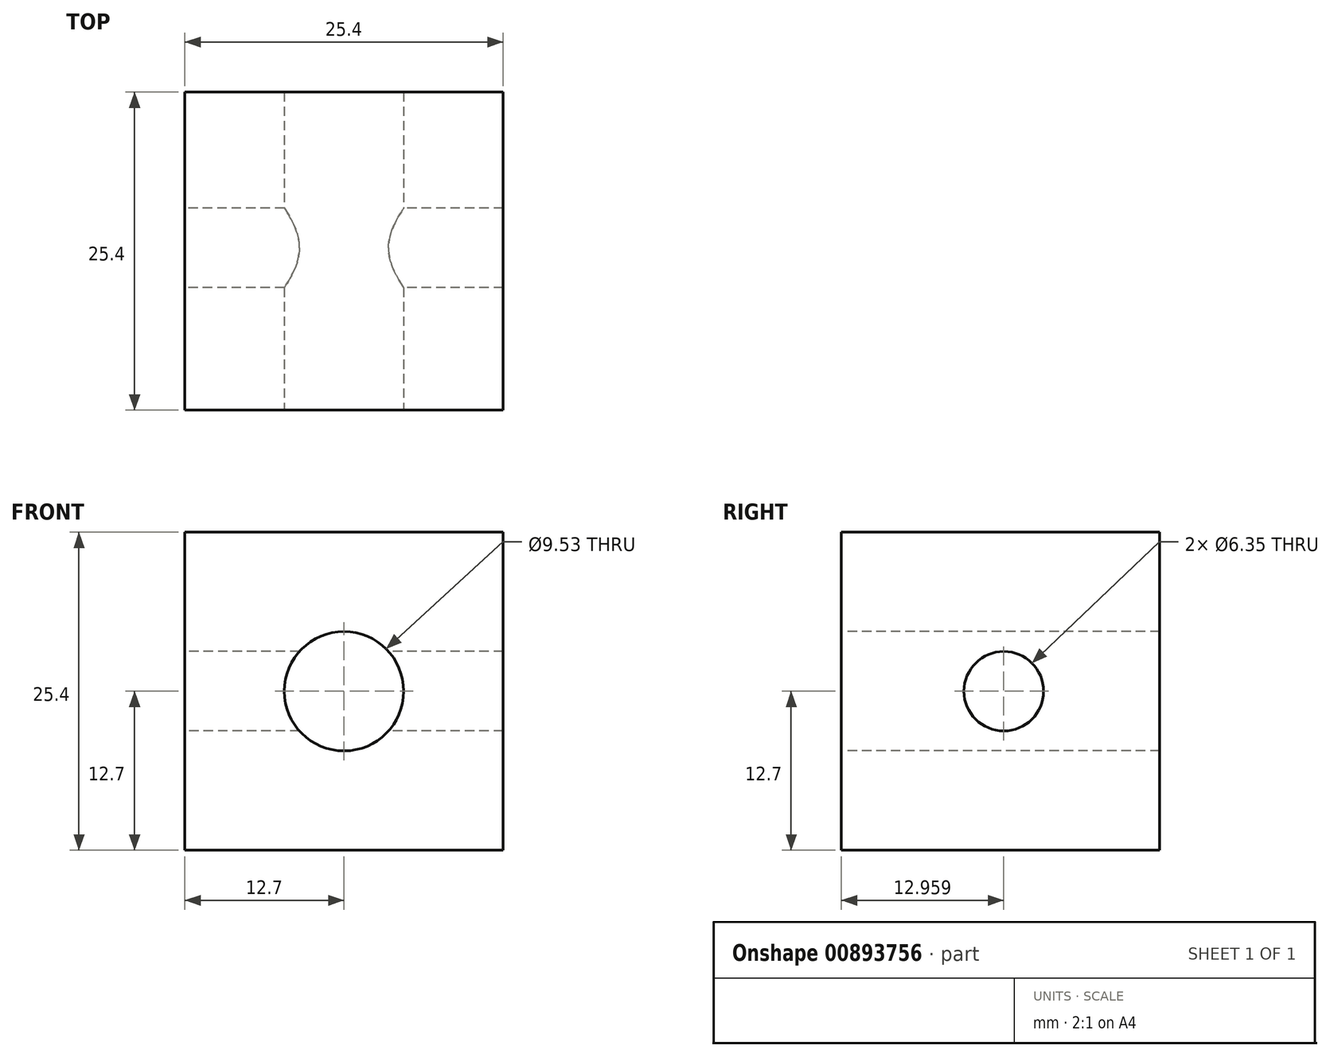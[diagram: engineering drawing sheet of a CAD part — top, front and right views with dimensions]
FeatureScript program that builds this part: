
annotation { "Feature Type Name" : "Feature", "Feature Type Description" : "" }
export const myFeature = defineFeature(function(context is Context, id is Id, definition is map)
    precondition{}
    {
        {
            var Q0;
            Q0=qCreatedBy(makeId("Front.planeOp"),FACE);
            var sketch = newSketch(context, id + "F0", { "sketchPlane" : qUnion([Q0])});
            skLineSegment(sketch, "E0.bottom", {"start": v(12.7, -12.7) * mm, "end": v(-12.7, -12.7) * mm});
            skLineSegment(sketch, "E0.top", {"start": v(12.7, 12.7) * mm, "end": v(-12.7, 12.7) * mm});
            skLineSegment(sketch, "E0.left", {"start": v(12.7, -12.7) * mm, "end": v(12.7, 12.7) * mm});
            skLineSegment(sketch, "E0.right", {"start": v(-12.7, -12.7) * mm, "end": v(-12.7, 12.7) * mm});
            skPoint(sketch, "E0.middle", {"position": v(0, 0) * mm});
            skSolve(sketch);
        }
        {
            var Q0;
            Q0 = qSketchRegion(id + "F0", true);
            extrude(context, id + "F1", {"entities" : qUnion([Q0]), "depth" : 25.4 * mm, "offsetDistance" : 25.4 * mm});
        }
        {
            var Q0;
            Q0=makeQuery(id+"F1.opExtrude","CAP_FACE",FACE,{"disambiguationData":[OSD([sQuery(id+"F0.wireOp",EDGE,"E0.bottom"),sQuery(id+"F0.wireOp",EDGE,"E0.top"),sQuery(id+"F0.wireOp",EDGE,"E0.left"),sQuery(id+"F0.wireOp",EDGE,"E0.right")])],"isStart":false});
            var sketch = newSketch(context, id + "F2", { "sketchPlane" : qUnion([Q0])});
            skCircle(sketch, "E1", {"center": v(0, 0) * mm, "radius": 4.76 * mm});
            skSolve(sketch);
        }
        {
            var Q0;
            Q0 = qSketchRegion(id + "F2", true);
            extrude(context, id + "F3", {"entities" : qUnion([Q0]), "operationType" : NewBodyOperationType.REMOVE, "oppositeDirection" : true, "depth" : 64.52 * mm, "offsetDistance" : 25.4 * mm});
        }
        {
            var Q0;
            Q0=makeQuery(id+"F1.opExtrude","SWEPT_FACE",FACE,{"disambiguationData":[OSD([sQuery(id+"F0.wireOp",EDGE,"E0.right")])]});
            var sketch = newSketch(context, id + "F4", { "sketchPlane" : qUnion([Q0])});
            skCircle(sketch, "E2", {"center": v(12.44, 0) * mm, "radius": 3.18 * mm});
            skSolve(sketch);
        }
        {
            var Q0;
            Q0 = qSketchRegion(id + "F4", true);
            extrude(context, id + "F5", {"entities" : qUnion([Q0]), "operationType" : NewBodyOperationType.REMOVE, "oppositeDirection" : true, "depth" : 53.6 * mm, "offsetDistance" : 25.4 * mm});
        }
    });
